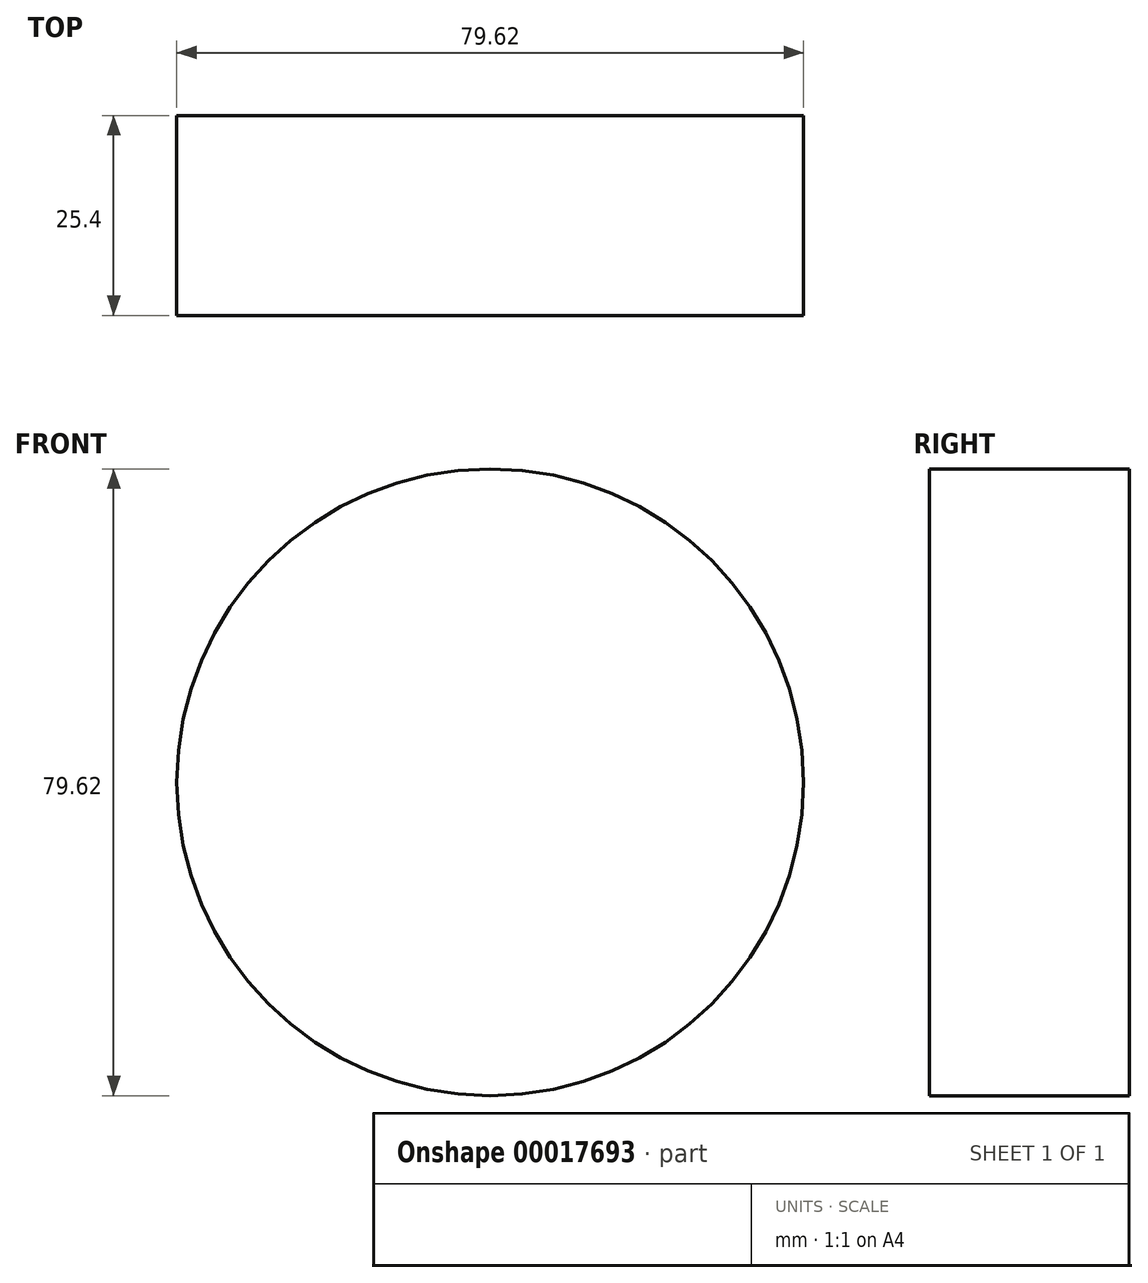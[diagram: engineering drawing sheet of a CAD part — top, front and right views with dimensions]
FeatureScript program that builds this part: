
annotation { "Feature Type Name" : "Feature", "Feature Type Description" : "" }
export const myFeature = defineFeature(function(context is Context, id is Id, definition is map)
    precondition{}
    {
        {
            var Q0;
            Q0=qCreatedBy(makeId("Front.planeOp"),FACE);
            var sketch = newSketch(context, id + "F0", { "sketchPlane" : qUnion([Q0])});
            skCircle(sketch, "E0", {"center": v(0, 0) * mm, "radius": 39.8 * mm});
            skSolve(sketch);
        }
        {
            var Q0;
            Q0=makeQuery(id+"F0.imprint","IMPRINT",FACE,{"disambiguationData":[TD([[makeQuery(id+"F0.imprint","IMPRINT",EDGE,{"derivedFrom":sQuery(id+"F0.wireOp",EDGE,"E0")}),1.0]])]});
            extrude(context, id + "F1", {"entities" : qUnion([Q0]), "endBound" : BoundingType.SYMMETRIC, "depth" : 25.4 * mm});
        }
    });
